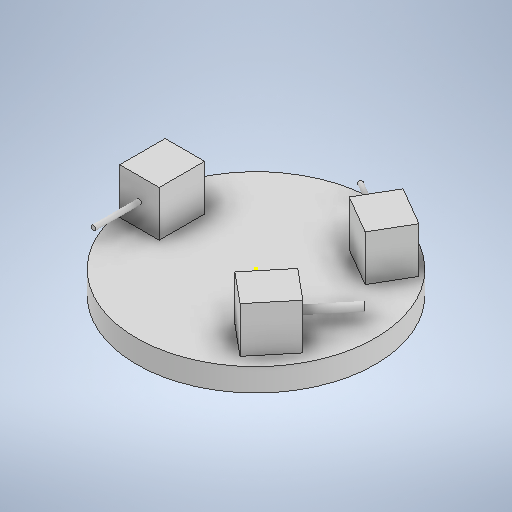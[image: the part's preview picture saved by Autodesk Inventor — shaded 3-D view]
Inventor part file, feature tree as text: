
AUTODESK INVENTOR PART (.ipt)
format: ipt  version: 2025 (Build 290162000, 162)  size: 267,776 bytes
history: native  units: in
note: dims shown in document units (in); Inventor stores cm internally (conversion verified against a paired STEP export)
features: sketch x6, extrude x5
ambient origin geometry x8: Origin, YZ Plane, XZ Plane, XY Plane, X Axis, Y Axis, Z Axis, Center Point
bodies: Solid1 (feature_tree)
feature tree (11):
  extrude  "Extrusion1"  Depth=0.2in TaperAngle=0.0deg
  extrude  "Extrusion2"  Depth=0.2in TaperAngle=0.0deg
  extrude  "Extrusion3"  [1 undecoded]
  extrude  "Extrusion4"  [1 undecoded]
  extrude  "Extrusion5"  [1 undecoded]
  sketch  "Sketch6"
  sketch  "Sketch1"  dims[d1=0.1in d2=0.0in d3=0.2in d4=0.0in]
  sketch  "Sketch2"  dims[d5=0.2in d6=0.0in d7=0.2in d8=0.0in]
  sketch  "Sketch3"  dims[d9=0.2in d10=0.0in]
  sketch  "Sketch4"
  sketch  "Sketch5"
note: 3 required parameter values undecoded (feature->parameter linkage not recoverable at this tier; creation-order binding heuristic only, values carry confidence <= 0.55)
